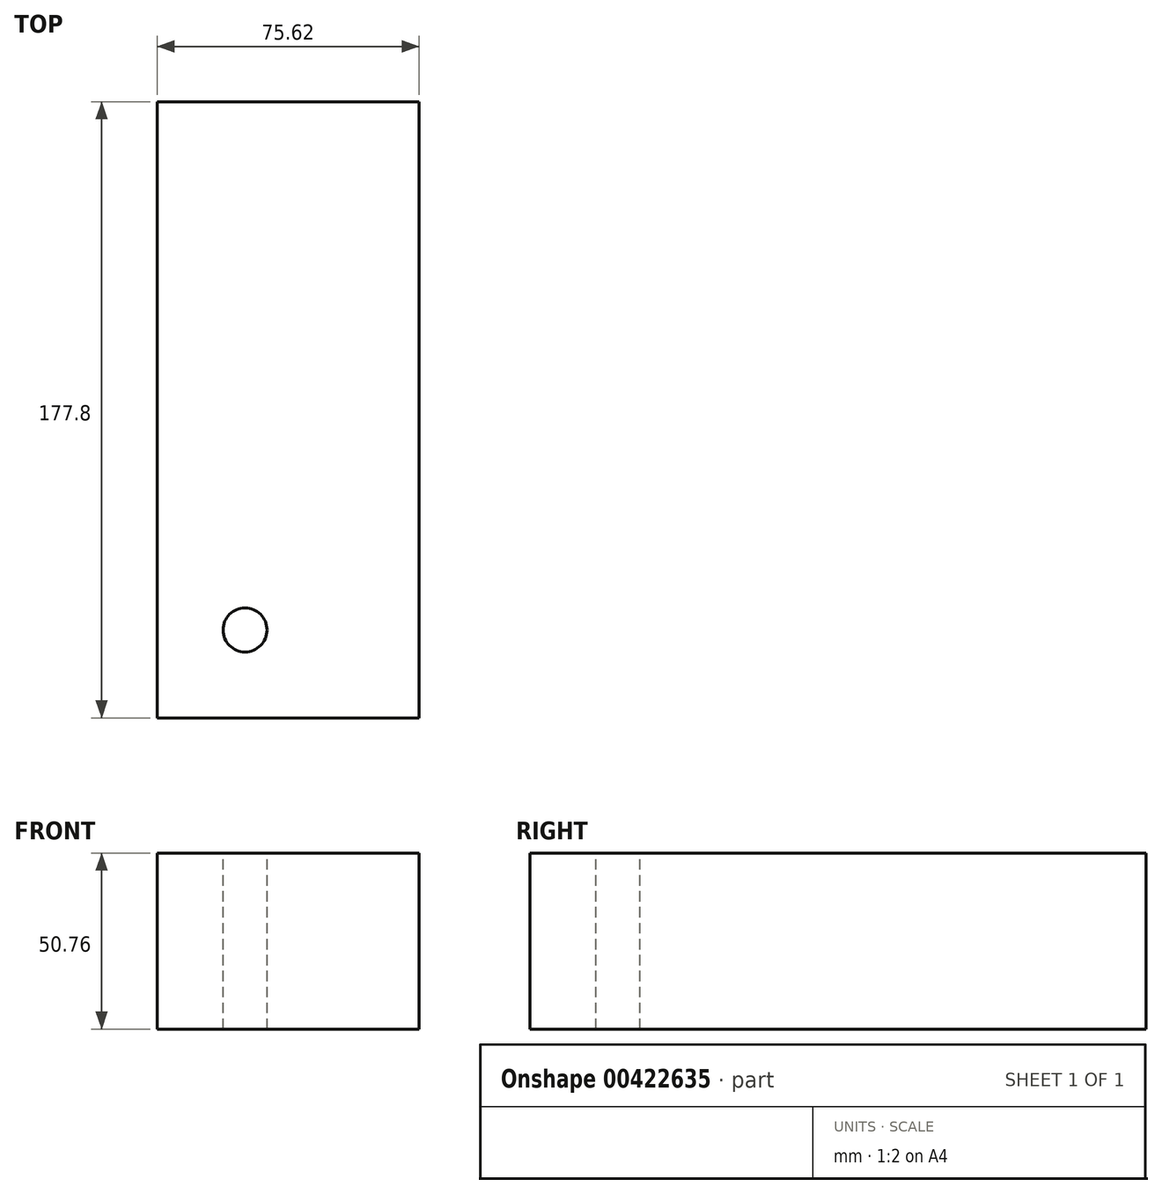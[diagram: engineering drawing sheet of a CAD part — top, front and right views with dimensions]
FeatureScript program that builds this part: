
annotation { "Feature Type Name" : "Feature", "Feature Type Description" : "" }
export const myFeature = defineFeature(function(context is Context, id is Id, definition is map)
    precondition{}
    {
        {
            var Q0;
            Q0=qCreatedBy(makeId("Front.planeOp"),FACE);
            var sketch = newSketch(context, id + "F0", { "sketchPlane" : qUnion([Q0])});
            skLineSegment(sketch, "E0.bottom", {"start": v(0, 0) * mm, "end": v(75.62, 0) * mm});
            skLineSegment(sketch, "E0.top", {"start": v(0, 50.76) * mm, "end": v(75.62, 50.76) * mm});
            skLineSegment(sketch, "E0.left", {"start": v(0, 0) * mm, "end": v(0, 50.76) * mm});
            skLineSegment(sketch, "E0.right", {"start": v(75.62, 0) * mm, "end": v(75.62, 50.76) * mm});
            skSolve(sketch);
        }
        {
            var Q0;
            Q0 = qSketchRegion(id + "F0", true);
            extrude(context, id + "F1", {"entities" : qUnion([Q0]), "depth" : 177.8 * mm});
        }
        {
            var Q0;
            Q0=makeQuery(id+"F1.opExtrude","SWEPT_FACE",FACE,{"disambiguationData":[OSD([sQuery(id+"F0.wireOp",EDGE,"E0.top")])]});
            var sketch = newSketch(context, id + "F2", { "sketchPlane" : qUnion([Q0])});
            skCircle(sketch, "E1", {"center": v(25.4, -152.4) * mm, "radius": 6.35 * mm});
            skSolve(sketch);
        }
        {
            var Q0;
            Q0 = qSketchRegion(id + "F2", true);
            extrude(context, id + "F3", {"entities" : qUnion([Q0]), "operationType" : NewBodyOperationType.REMOVE, "endBound" : BoundingType.THROUGH_ALL, "oppositeDirection" : true, "depth" : 25.4 * mm});
        }
    });
